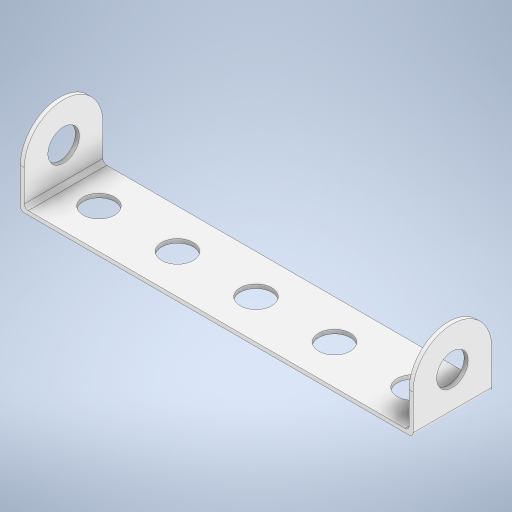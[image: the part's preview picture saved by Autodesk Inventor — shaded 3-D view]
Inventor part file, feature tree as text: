
AUTODESK INVENTOR PART (.ipt)
format: ipt  version: 2024 (Build 280153000, 153)  size: 311,808 bytes
history: native  units: mm
features: extrude x4, sketch x4, pattern_linear x2, fillet x2, other x1
ambient origin geometry x8: Origin, YZ Plane, XZ Plane, XY Plane, X Axis, Y Axis, Z Axis, Center Point
bodies: Body1 (feature_tree)
feature tree (13):
  other  "Těleso1"
  extrude  "Vysunutí1"  Depth=25.0mm
  extrude  "Vysunutí2"  Depth=25.0mm
  pattern_linear  "Obdélníkové pole1"  Spacing1=0.5mm  [1 undecoded]
  extrude  "Vysunutí3"  Depth=0.5mm
  pattern_linear  "Obdélníkové pole2"  Spacing1=0.5mm  [1 undecoded]
  extrude  "Vysunutí4"  Depth=10.0mm
  fillet  "Zaoblení1"  Radius=10.0mm
  fillet  "Zaoblení2"  Radius=10.0mm
  sketch  "Náčrt1"
  sketch  "Náčrt2"
  sketch  "Náčrt3"
  sketch  "Náčrt4"
note: 2 required parameter values undecoded (feature->parameter linkage not recoverable at this tier; creation-order binding heuristic only, values carry confidence <= 0.55)
